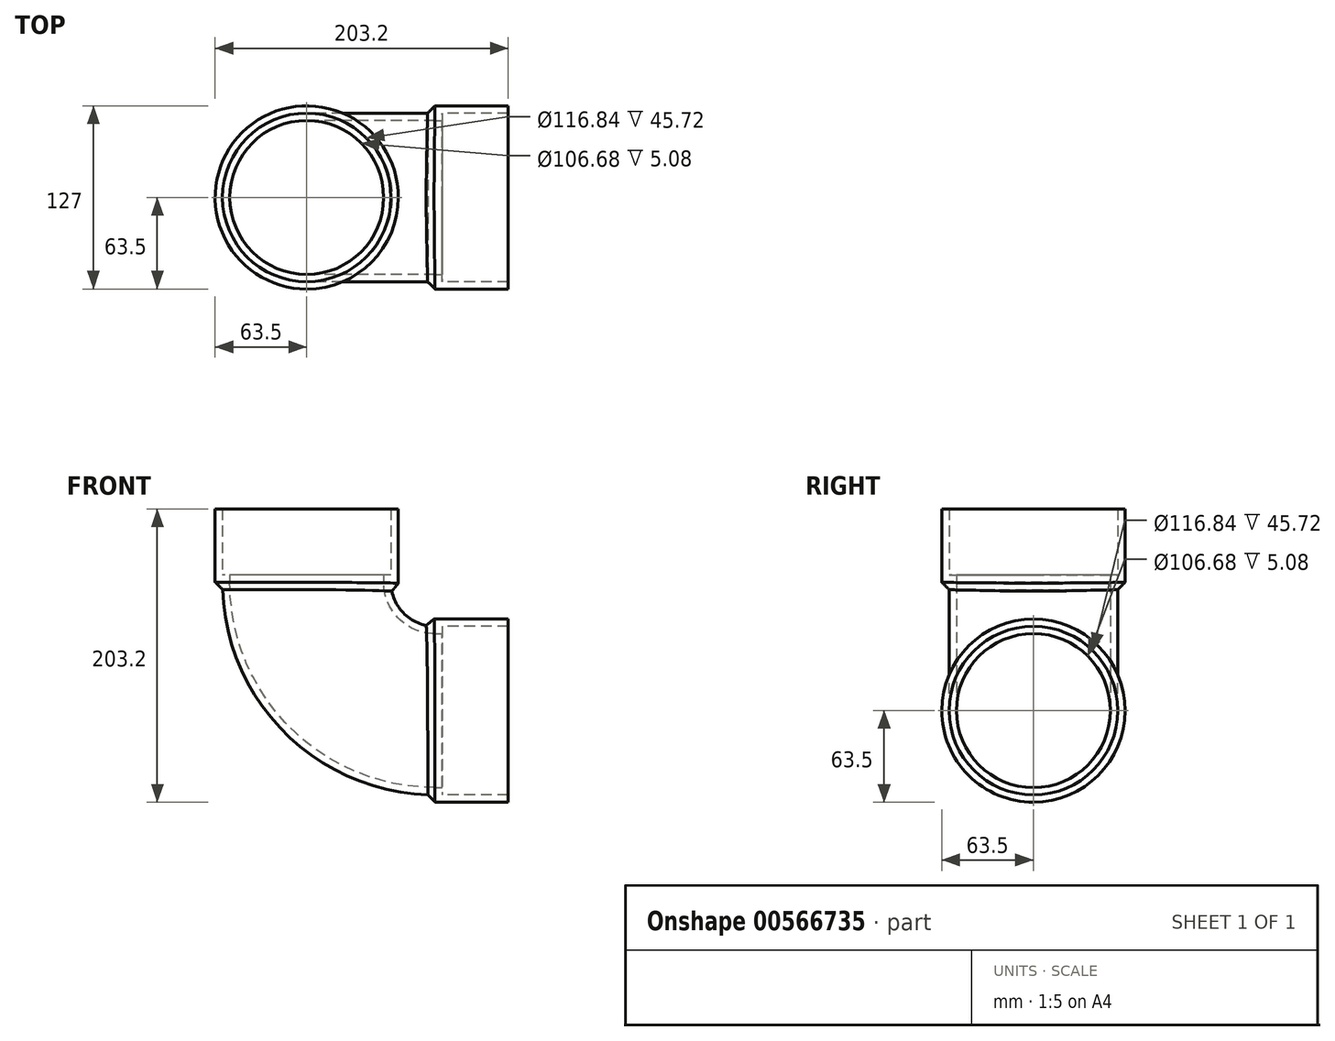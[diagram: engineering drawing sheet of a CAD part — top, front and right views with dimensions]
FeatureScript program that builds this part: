
annotation { "Feature Type Name" : "Feature", "Feature Type Description" : "" }
export const myFeature = defineFeature(function(context is Context, id is Id, definition is map)
    precondition{}
    {
        {
            var Q0;
            Q0=qCreatedBy(makeId("Top.planeOp"),FACE);
            var sketch = newSketch(context, id + "F0", { "sketchPlane" : qUnion([Q0])});
            skCircle(sketch, "E0", {"center": v(0, 0) * mm, "radius": 63.5 * mm});
            skLineSegment(sketch, "E1", {"start": v(88.9, 40) * mm, "end": v(88.9, -35.24) * mm});
            skSolve(sketch);
        }
        {
            var Q0;
            Q0=makeQuery(id+"F0.imprint","IMPRINT",FACE,{"disambiguationData":[TD([[makeQuery(id+"F0.imprint","IMPRINT",EDGE,{"derivedFrom":sQuery(id+"F0.wireOp",EDGE,"E0")}),1.0]])]});
            var Q1;
            Q1=makeQuery(id+"F0.imprint","IMPRINT",FACE,{"disambiguationData":[TD([[makeQuery(id+"F0.imprint","IMPRINT",EDGE,{"derivedFrom":sQuery(id+"F0.wireOp",EDGE,"4vr16HTV-bw5p-N6pc-xBq0-Ipfc8GHGUd3C")}),1.0]])]});
            extrude(context, id + "F1", {"entities" : qUnion([Q0, Q1]), "depth" : 50.8 * mm, "offsetDistance" : 25.4 * mm});
        }
        {
            var Q0;
            Q0=qCreatedBy(makeId("Top.planeOp"),FACE);
            var sketch = newSketch(context, id + "F2", { "sketchPlane" : qUnion([Q0])});
            skCircle(sketch, "E2", {"center": v(0, 0) * mm, "radius": 58.42 * mm});
            skSolve(sketch);
        }
        {
            var Q0;
            Q0=makeQuery(id+"F2.imprint","IMPRINT",FACE,{"disambiguationData":[TD([[makeQuery(id+"F2.imprint","IMPRINT",EDGE,{"derivedFrom":sQuery(id+"F2.wireOp",EDGE,"E2")}),1.0]])]});
            extrude(context, id + "F3", {"entities" : qUnion([Q0]), "operationType" : NewBodyOperationType.REMOVE, "endBound" : BoundingType.SYMMETRIC, "depth" : 101.6 * mm, "offsetDistance" : 25.4 * mm});
        }
        {
            var Q0;
            Q0=qSketchRegion(id+"F2",true);
            var Q1;
            Q1=sQuery(id+"F0.wireOp",EDGE,"E1");
            revolve(context, id + "F4", {"operationType" : NewBodyOperationType.ADD, "surfaceOperationType" : NewSurfaceOperationType.NEW, "entities" : qUnion([Q0]), "axis" : qUnion([Q1]), "revolveType" : RevolveType.ONE_DIRECTION, "angle" : 90 * degree});
        }
        {
            var Q0;
            Q0=makeQuery(id+"F2.imprint","IMPRINT",FACE,{"disambiguationData":[TD([[makeQuery(id+"F2.imprint","IMPRINT",EDGE,{"derivedFrom":sQuery(id+"F2.wireOp",EDGE,"E2")}),1.0]])]});
            extrude(context, id + "F5", {"entities" : qUnion([Q0]), "operationType" : NewBodyOperationType.ADD, "depth" : 5.08 * mm, "offsetDistance" : 25.4 * mm});
        }
        {
            var Q0;
            Q0=makeQuery(id+"F4.opRevolve","CAP_FACE",FACE,{"disambiguationData":[OSD([sQuery(id+"F2.wireOp",EDGE,"E2")])],"isStart":false});
            var sketch = newSketch(context, id + "F6", { "sketchPlane" : qUnion([Q0])});
            skPoint(sketch, "E3", {"position": v(0, -88.9) * mm});
            skCircle(sketch, "E4", {"center": v(0, -88.9) * mm, "radius": 58.42 * mm});
            skSolve(sketch);
        }
        {
            var Q0;
            Q0=makeQuery(id+"F6.imprint","IMPRINT",FACE,{"disambiguationData":[TD([[makeQuery(id+"F6.imprint","IMPRINT",EDGE,{"derivedFrom":sQuery(id+"F6.wireOp",EDGE,"E4")}),-1.0]])]});
            var sketch = newSketch(context, id + "F7", { "sketchPlane" : qUnion([Q0])});
            skPoint(sketch, "E5", {"position": v(0, -88.9) * mm});
            skCircle(sketch, "E6", {"center": v(0, -88.9) * mm, "radius": 63.5 * mm});
            skSolve(sketch);
        }
        {
            var Q0;
            Q0=makeQuery(id+"F6.imprint","IMPRINT",FACE,{"disambiguationData":[TD([[makeQuery(id+"F6.imprint","IMPRINT",EDGE,{"derivedFrom":sQuery(id+"F6.wireOp",EDGE,"E4")}),-1.0]])]});
            extrude(context, id + "F8", {"entities" : qUnion([Q0]), "operationType" : NewBodyOperationType.ADD, "depth" : 5.08 * mm, "offsetDistance" : 25.4 * mm});
        }
        {
            var Q0;
            Q0=makeQuery(id+"F7.imprint","IMPRINT",FACE,{"disambiguationData":[TD([[makeQuery(id+"F7.imprint","IMPRINT",EDGE,{"derivedFrom":sQuery(id+"F7.wireOp",EDGE,"E6")}),1.0]])]});
            extrude(context, id + "F9", {"entities" : qUnion([Q0]), "operationType" : NewBodyOperationType.ADD, "depth" : 50.8 * mm, "offsetDistance" : 25.4 * mm});
        }
        {
            var Q0;
            Q0=qCreatedBy(makeId("Top.planeOp"),FACE);
            var sketch = newSketch(context, id + "F10", { "sketchPlane" : qUnion([Q0])});
            skCircle(sketch, "E7", {"center": v(0, 0) * mm, "radius": 53.34 * mm});
            skSolve(sketch);
        }
        {
            var Q0;
            Q0=qSketchRegion(id+"F10",true);
            extrude(context, id + "F11", {"entities" : qUnion([Q0]), "operationType" : NewBodyOperationType.REMOVE, "oppositeDirection" : true, "depth" : -25.4 * mm, "offsetDistance" : 25.4 * mm});
        }
        {
            var Q0;
            Q0=qSketchRegion(id+"F10",true);
            var Q1;
            Q1=sQuery(id+"F0.wireOp",EDGE,"E1");
            revolve(context, id + "F12", {"operationType" : NewBodyOperationType.REMOVE, "surfaceOperationType" : NewSurfaceOperationType.NEW, "entities" : qUnion([Q0]), "axis" : qUnion([Q1]), "revolveType" : RevolveType.ONE_DIRECTION, "angle" : 90 * degree});
        }
        {
            var Q0;
            Q0=makeQuery(id+"F8.opExtrude","CAP_FACE",FACE,{"disambiguationData":[OSD([sQuery(id+"F6.wireOp",EDGE,"E4")])],"isStart":false});
            var sketch = newSketch(context, id + "F13", { "sketchPlane" : qUnion([Q0])});
            skCircle(sketch, "E8", {"center": v(0, -88.9) * mm, "radius": 53.34 * mm});
            skSolve(sketch);
        }
        {
            var Q0;
            Q0=qSketchRegion(id+"F13",true);
            extrude(context, id + "F14", {"entities" : qUnion([Q0]), "operationType" : NewBodyOperationType.REMOVE, "oppositeDirection" : true, "depth" : 5.08 * mm, "offsetDistance" : 25.4 * mm});
        }
        {
            var Q0;
            {var subQ0=sQuery(id+"F2.wireOp",EDGE,"E2");Q0=makeQuery(id+"F5.boolean.opBoolean","MERGE",EDGE,{"derivedFrom":[makeQuery(id+"F3.boolean.opBoolean","INTERSECT",EDGE,{"derivedFrom":[makeQuery(id+"F1.opExtrude","CAP_FACE",FACE,{"disambiguationData":[OSD([sQuery(id+"F0.wireOp",EDGE,"E0")])],"isStart":true}),makeQuery(id+"F3.opExtrude","SWEPT_FACE",FACE,{"disambiguationData":[OSD([subQ0])]})]}),makeQuery(id+"F4.opRevolve","CAP_EDGE",EDGE,{"disambiguationData":[OSD([subQ0])],"isStart":true}),makeQuery(id+"F5.opExtrude","CAP_EDGE",EDGE,{"disambiguationData":[OSD([subQ0])],"isStart":true})]});}
            var Q1;
            {var subQ0=sQuery(id+"F6.wireOp",EDGE,"E4");Q1=makeQuery(id+"F9.boolean.opBoolean","MERGE",EDGE,{"derivedFrom":[makeQuery(id+"F8.boolean.opBoolean","MERGE",EDGE,{"derivedFrom":[makeQuery(id+"F4.opRevolve","CAP_EDGE",EDGE,{"disambiguationData":[OSD([sQuery(id+"F2.wireOp",EDGE,"E2")])],"isStart":false}),makeQuery(id+"F8.opExtrude","CAP_EDGE",EDGE,{"disambiguationData":[OSD([subQ0])],"isStart":true})]}),makeQuery(id+"F9.opExtrude","CAP_EDGE",EDGE,{"disambiguationData":[OSD([subQ0])],"isStart":true})]});}
            chamfer(context, id + "F15", {"entities" : qUnion([Q0, Q1]), "width" : 5.08 * mm, "tangentPropagation" : true});
        }
    });
